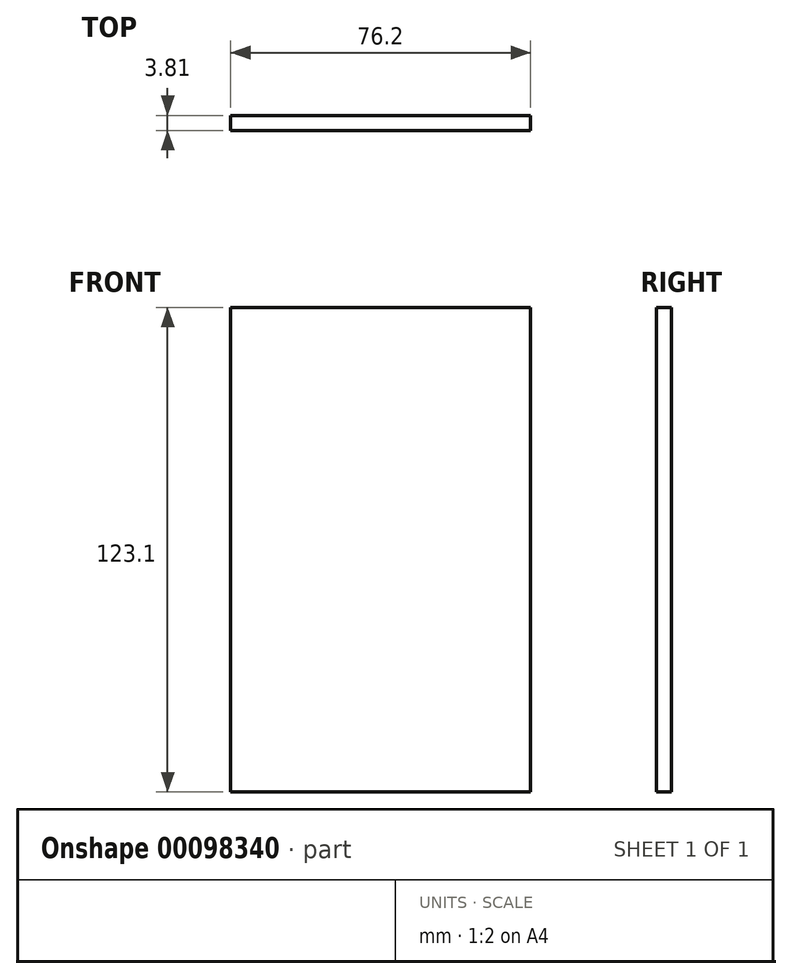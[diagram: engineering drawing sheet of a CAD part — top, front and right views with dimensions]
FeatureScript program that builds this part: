
annotation { "Feature Type Name" : "Feature", "Feature Type Description" : "" }
export const myFeature = defineFeature(function(context is Context, id is Id, definition is map)
    precondition{}
    {
        {
            var Q0;
            Q0=qCreatedBy(makeId("Front.planeOp"),FACE);
            var sketch = newSketch(context, id + "F0", { "sketchPlane" : qUnion([Q0])});
            skLineSegment(sketch, "E0.bottom", {"start": v(-38.1, 61.55) * mm, "end": v(38.1, 61.55) * mm});
            skLineSegment(sketch, "E0.top", {"start": v(-38.1, -61.55) * mm, "end": v(38.1, -61.55) * mm});
            skLineSegment(sketch, "E0.left", {"start": v(-38.1, 61.55) * mm, "end": v(-38.1, -61.55) * mm});
            skLineSegment(sketch, "E0.right", {"start": v(38.1, 61.55) * mm, "end": v(38.1, -61.55) * mm});
            skPoint(sketch, "E0.middle", {"position": v(0, 0) * mm});
            skSolve(sketch);
        }
        {
            var Q0;
            Q0 = qSketchRegion(id + "F0", true);
            extrude(context, id + "F1", {"entities" : qUnion([Q0]), "depth" : 3.8 * mm});
        }
    });
